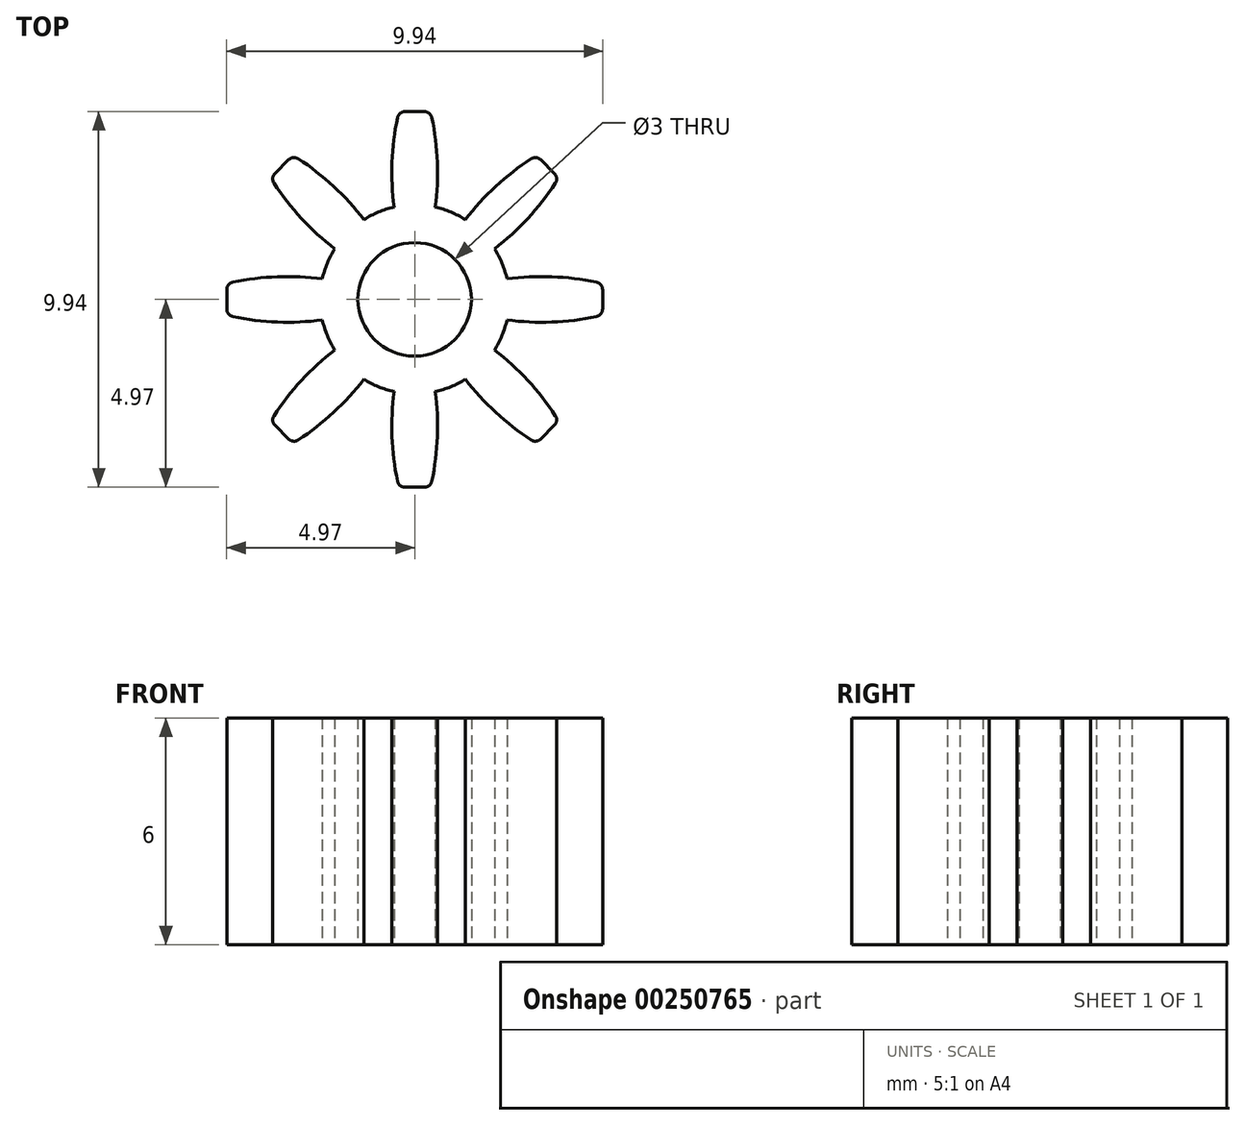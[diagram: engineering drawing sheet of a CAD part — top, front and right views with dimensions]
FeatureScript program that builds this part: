
annotation { "Feature Type Name" : "Feature", "Feature Type Description" : "" }
export const myFeature = defineFeature(function(context is Context, id is Id, definition is map)
    precondition{}
    {
        {
            var Q0;
            Q0=qCreatedBy(makeId("Top.planeOp"),FACE);
            var sketch = newSketch(context, id + "F0", { "sketchPlane" : qUnion([Q0])});
            skCircle(sketch, "E0", {"center": v(0, 0) * mm, "radius": 5 * mm, "construction": true});
            skCircle(sketch, "E1", {"center": v(0, 0) * mm, "radius": 1.5 * mm});
            skLineSegment(sketch, "E2", {"start": v(0, 0) * mm, "end": v(0, 5) * mm, "construction": true});
            skLineSegment(sketch, "E3", {"start": v(0, 3.6) * mm, "end": v(0.6, 3.6) * mm, "construction": true});
            skArc(sketch, "E4", {"start": v(0.54, 2.44) * mm, "mid": v(0.6, 3.63) * mm, "end": v(0.45, 4.8) * mm});
            skArc(sketch, "E5.MirrorCS", {"start": v(-0.54, 2.44) * mm, "mid": v(-0.6, 3.63) * mm, "end": v(-0.45, 4.8) * mm});
            skLineSegment(sketch, "E6", {"start": v(-0.26, 4.97) * mm, "end": v(0.26, 4.97) * mm});
            skPoint(sketch, "E7.visualSharp", {"position": v(-0.42, 4.97) * mm});
            skArc(sketch, "E7.filletArc", {"start": v(-0.26, 4.97) * mm, "mid": v(-0.38, 4.92) * mm, "end": v(-0.45, 4.8) * mm});
            skPoint(sketch, "E8.visualSharp", {"position": v(0.42, 4.97) * mm});
            skArc(sketch, "E8.filletArc", {"start": v(0.45, 4.8) * mm, "mid": v(0.38, 4.92) * mm, "end": v(0.26, 4.97) * mm});
            skArc(sketch, "E9.1.0", {"start": v(-1.34, 2.11) * mm, "mid": v(-2.14, 2.99) * mm, "end": v(-3.08, 3.72) * mm});
            skArc(sketch, "E9.1.1", {"start": v(-3.08, 3.72) * mm, "mid": v(-3.2, 3.75) * mm, "end": v(-3.33, 3.7) * mm});
            skLineSegment(sketch, "E9.1.2", {"start": v(-3.7, 3.33) * mm, "end": v(-3.33, 3.7) * mm});
            skArc(sketch, "E9.1.3", {"start": v(-3.7, 3.33) * mm, "mid": v(-3.75, 3.2) * mm, "end": v(-3.72, 3.08) * mm});
            skArc(sketch, "E9.1.4", {"start": v(-2.11, 1.34) * mm, "mid": v(-2.99, 2.14) * mm, "end": v(-3.72, 3.08) * mm});
            skArc(sketch, "E9.2.0", {"start": v(-2.44, 0.54) * mm, "mid": v(-3.63, 0.6) * mm, "end": v(-4.8, 0.45) * mm});
            skArc(sketch, "E9.2.1", {"start": v(-4.8, 0.45) * mm, "mid": v(-4.92, 0.38) * mm, "end": v(-4.97, 0.26) * mm});
            skLineSegment(sketch, "E9.2.2", {"start": v(-4.97, -0.26) * mm, "end": v(-4.97, 0.26) * mm});
            skArc(sketch, "E9.2.3", {"start": v(-4.97, -0.26) * mm, "mid": v(-4.92, -0.38) * mm, "end": v(-4.8, -0.45) * mm});
            skArc(sketch, "E9.2.4", {"start": v(-2.44, -0.54) * mm, "mid": v(-3.63, -0.6) * mm, "end": v(-4.8, -0.45) * mm});
            skArc(sketch, "E9.3.0", {"start": v(-2.11, -1.34) * mm, "mid": v(-2.99, -2.14) * mm, "end": v(-3.72, -3.08) * mm});
            skArc(sketch, "E9.3.1", {"start": v(-3.72, -3.08) * mm, "mid": v(-3.75, -3.2) * mm, "end": v(-3.7, -3.33) * mm});
            skLineSegment(sketch, "E9.3.2", {"start": v(-3.33, -3.7) * mm, "end": v(-3.7, -3.33) * mm});
            skArc(sketch, "E9.3.3", {"start": v(-3.33, -3.7) * mm, "mid": v(-3.2, -3.75) * mm, "end": v(-3.08, -3.72) * mm});
            skArc(sketch, "E9.3.4", {"start": v(-1.34, -2.11) * mm, "mid": v(-2.14, -2.99) * mm, "end": v(-3.08, -3.72) * mm});
            skArc(sketch, "E9.4.0", {"start": v(-0.54, -2.44) * mm, "mid": v(-0.6, -3.63) * mm, "end": v(-0.45, -4.8) * mm});
            skArc(sketch, "E9.4.1", {"start": v(-0.45, -4.8) * mm, "mid": v(-0.38, -4.92) * mm, "end": v(-0.26, -4.97) * mm});
            skLineSegment(sketch, "E9.4.2", {"start": v(0.26, -4.97) * mm, "end": v(-0.26, -4.97) * mm});
            skArc(sketch, "E9.4.3", {"start": v(0.26, -4.97) * mm, "mid": v(0.38, -4.92) * mm, "end": v(0.45, -4.8) * mm});
            skArc(sketch, "E9.4.4", {"start": v(0.54, -2.44) * mm, "mid": v(0.6, -3.63) * mm, "end": v(0.45, -4.8) * mm});
            skArc(sketch, "E9.5.0", {"start": v(1.34, -2.11) * mm, "mid": v(2.14, -2.99) * mm, "end": v(3.08, -3.72) * mm});
            skArc(sketch, "E9.5.1", {"start": v(3.08, -3.72) * mm, "mid": v(3.2, -3.75) * mm, "end": v(3.33, -3.7) * mm});
            skLineSegment(sketch, "E9.5.2", {"start": v(3.7, -3.33) * mm, "end": v(3.33, -3.7) * mm});
            skArc(sketch, "E9.5.3", {"start": v(3.7, -3.33) * mm, "mid": v(3.75, -3.2) * mm, "end": v(3.72, -3.08) * mm});
            skArc(sketch, "E9.5.4", {"start": v(2.11, -1.34) * mm, "mid": v(2.99, -2.14) * mm, "end": v(3.72, -3.08) * mm});
            skArc(sketch, "E9.6.0", {"start": v(2.44, -0.54) * mm, "mid": v(3.63, -0.6) * mm, "end": v(4.8, -0.45) * mm});
            skArc(sketch, "E9.6.1", {"start": v(4.8, -0.45) * mm, "mid": v(4.92, -0.38) * mm, "end": v(4.97, -0.26) * mm});
            skLineSegment(sketch, "E9.6.2", {"start": v(4.97, 0.26) * mm, "end": v(4.97, -0.26) * mm});
            skArc(sketch, "E9.6.3", {"start": v(4.97, 0.26) * mm, "mid": v(4.92, 0.38) * mm, "end": v(4.8, 0.45) * mm});
            skArc(sketch, "E9.6.4", {"start": v(2.44, 0.54) * mm, "mid": v(3.63, 0.6) * mm, "end": v(4.8, 0.45) * mm});
            skArc(sketch, "E9.7.0", {"start": v(2.11, 1.34) * mm, "mid": v(2.99, 2.14) * mm, "end": v(3.72, 3.08) * mm});
            skArc(sketch, "E9.7.1", {"start": v(3.72, 3.08) * mm, "mid": v(3.75, 3.2) * mm, "end": v(3.7, 3.33) * mm});
            skLineSegment(sketch, "E9.7.2", {"start": v(3.33, 3.7) * mm, "end": v(3.7, 3.33) * mm});
            skArc(sketch, "E9.7.3", {"start": v(3.33, 3.7) * mm, "mid": v(3.2, 3.75) * mm, "end": v(3.08, 3.72) * mm});
            skArc(sketch, "E9.7.4", {"start": v(1.34, 2.11) * mm, "mid": v(2.14, 2.99) * mm, "end": v(3.08, 3.72) * mm});
            skArc(sketch, "E10", {"start": v(-0.54, 2.44) * mm, "mid": v(-0.96, 2.3) * mm, "end": v(-1.34, 2.11) * mm});
            skArc(sketch, "E11.trimOffspring", {"start": v(1.34, 2.11) * mm, "mid": v(0.96, 2.3) * mm, "end": v(0.54, 2.44) * mm});
            skArc(sketch, "E12.trimOffspring", {"start": v(2.44, 0.54) * mm, "mid": v(2.3, 0.96) * mm, "end": v(2.11, 1.34) * mm});
            skArc(sketch, "E13.trimOffspring", {"start": v(2.11, -1.34) * mm, "mid": v(2.3, -0.96) * mm, "end": v(2.44, -0.54) * mm});
            skArc(sketch, "E14.trimOffspring", {"start": v(0.54, -2.44) * mm, "mid": v(0.96, -2.3) * mm, "end": v(1.34, -2.11) * mm});
            skArc(sketch, "E15.trimOffspring", {"start": v(-1.34, -2.11) * mm, "mid": v(-0.96, -2.3) * mm, "end": v(-0.54, -2.44) * mm});
            skArc(sketch, "E16.trimOffspring", {"start": v(-2.44, -0.54) * mm, "mid": v(-2.3, -0.96) * mm, "end": v(-2.11, -1.34) * mm});
            skArc(sketch, "E17.trimOffspring", {"start": v(-2.11, 1.34) * mm, "mid": v(-2.3, 0.96) * mm, "end": v(-2.44, 0.54) * mm});
            skSolve(sketch);
        }
        {
            var Q0;
            Q0=makeQuery(id+"F0.imprint","IMPRINT",FACE,{"disambiguationData":[TD([[makeQuery(id+"F0.imprint","IMPRINT",EDGE,{"derivedFrom":sQuery(id+"F0.wireOp",EDGE,"E1")}),-1.0]])]});
            extrude(context, id + "F1", {"entities" : qUnion([Q0]), "depth" : 6 * mm});
        }
    });
